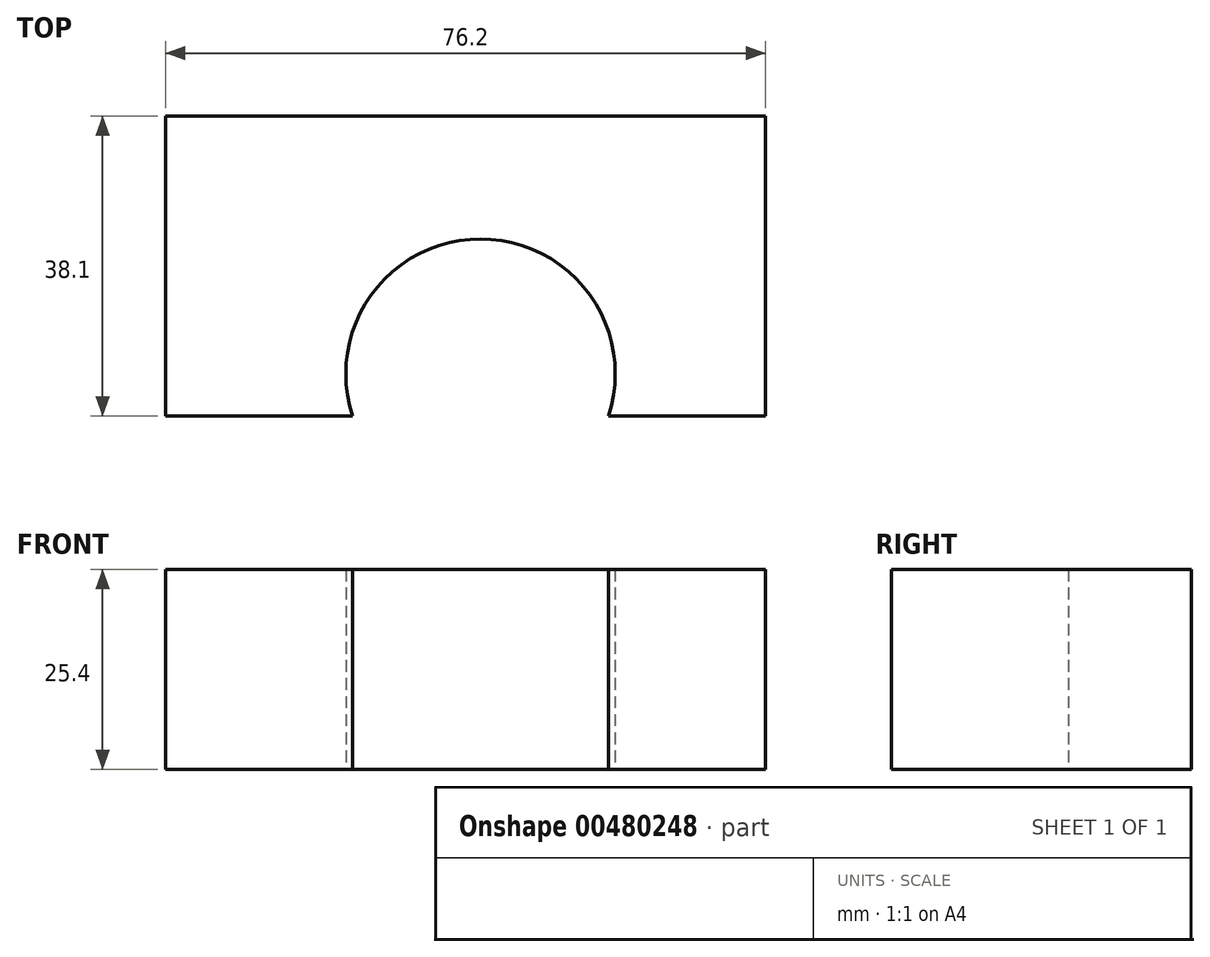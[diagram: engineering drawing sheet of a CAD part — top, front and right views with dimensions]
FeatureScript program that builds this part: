
annotation { "Feature Type Name" : "Feature", "Feature Type Description" : "" }
export const myFeature = defineFeature(function(context is Context, id is Id, definition is map)
    precondition{}
    {
        {
            var Q0;
            Q0=qCreatedBy(makeId("Top.planeOp"),FACE);
            var sketch = newSketch(context, id + "F0", { "sketchPlane" : qUnion([Q0])});
            skLineSegment(sketch, "E0.bottom", {"start": v(-42.71, 38.1) * mm, "end": v(33.49, 38.1) * mm});
            skLineSegment(sketch, "E0.top", {"start": v(-42.71, 0) * mm, "end": v(33.49, 0) * mm});
            skLineSegment(sketch, "E0.left", {"start": v(-42.71, 38.1) * mm, "end": v(-42.71, 0) * mm});
            skLineSegment(sketch, "E0.right", {"start": v(33.49, 38.1) * mm, "end": v(33.49, 0) * mm});
            skArc(sketch, "E1", {"start": v(13.54, 0) * mm, "mid": v(-2.7, 22.49) * mm, "end": v(-18.95, 0) * mm});
            skSolve(sketch);
        }
        {
            var Q0;
            Q0 = qSketchRegion(id + "F0", true);
            extrude(context, id + "F1", {"entities" : qUnion([Q0]), "depth" : 25.4 * mm, "offsetDistance" : 25.4 * mm});
        }
        {
            var Q0;
            {var subQ0=sQuery(id+"F0.wireOp",EDGE,"E1");Q0=makeQuery(id+"F0.imprint","IMPRINT",FACE,{"disambiguationData":[TD([[makeQuery(id+"F0.imprint","IMPRINT",EDGE,{"derivedFrom":subQ0}),1.0]])]});}
            extrude(context, id + "F2", {"entities" : qUnion([Q0]), "operationType" : NewBodyOperationType.REMOVE, "depth" : 25.4 * mm, "offsetDistance" : 25.4 * mm});
        }
    });
